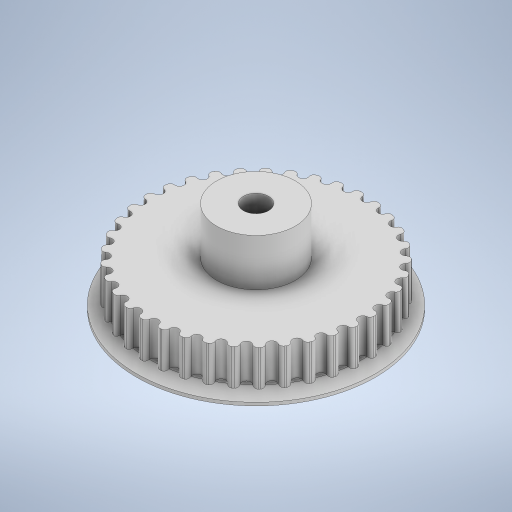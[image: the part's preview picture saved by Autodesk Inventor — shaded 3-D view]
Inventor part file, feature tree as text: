
AUTODESK INVENTOR PART (.ipt)
format: ipt  version: 2024 (Build 280153000, 153)  size: 653,312 bytes
history: native  units: mm
features: extrude x5, sketch x5, pattern_circular x1, fillet x1, chamfer x1
ambient origin geometry x8: Origin, YZ Plane, XZ Plane, XY Plane, X Axis, Y Axis, Z Axis, Center Point
bodies: Solid1 (feature_tree)
feature tree (13):
  extrude  "Extrusion1"  Depth=14.0mm TaperAngle=0.0deg
  extrude  "Extrusion2"  Depth=15.0mm TaperAngle=0.0deg
  extrude  "Extrusion3"  Depth=11.0mm TaperAngle=0.0deg
  pattern_circular  "Circular Pattern1"  Count=37 Angle=360.0deg
  fillet  "Fillet1"  Radius=1.2mm
  extrude  "Extrusion4"  Depth=4.0mm TaperAngle=45.0deg
  chamfer  "Chamfer1"  Distance=30.0mm
  extrude  "Extrusion5"  [1 undecoded]
  sketch  "Sketch1"  dims[d0=70.0mm d1=14.0mm d2=0.0mm]
  sketch  "Sketch2"  dims[d3=25.0mm d4=15.0mm d5=0.0mm]
  sketch  "Sketch3"  dims[d7=2.85mm d8=11.0mm d9=0.0mm d10=370.0mm d11=360.0deg d13=1.2mm]
  sketch  "Sketch4"  dims[d14=3.0mm d15=0.0mm d16=4.0mm d17=2.0mm d18=45.0deg d19=30.0mm d20=0.0mm]
  sketch  "Sketch5"
note: 1 required parameter value undecoded (feature->parameter linkage not recoverable at this tier; creation-order binding heuristic only, values carry confidence <= 0.55)
